# Revit family: tka-2200c-60_60Hz
name_source: partatom
category: 機械設備
units: mm (PartAtom-declared; Revit-internal decimal feet)

## family parameters
OmniClass タイトル = Heat Exchangers for Ventilation Air
OmniClass 番号 = 23.75.10.34.21
パーツ タイプ = 標準
ロード時にボイドで切り取り = いいえ
丸型コネクタ寸法 = 直径を使用
作業面ベース = いいえ
共有 = いいえ
常に垂直 = はい
部屋計算ポイント = はい

## types (1)
- TKA-2200C-60
    Clearance Front = 600
    Clearance Left = 600
    Clearance Top = 340  [stored 1.11549 ft]
    Depth = 897  [stored 2.94291 ft]
    EAサイズ_D = 0  [stored 0 ft]
    EAサイズ_W = 0  [stored 0 ft]
    Height = 380
    IfcExportAs = IfcAirToAirHeatRecoveryType
    IfcExportType = ROTARYWHEEL
    MAX静圧 = 0.0 Pa
    MAX風量 = 630.0 m³/h
    MIN静圧 = 0.0 Pa
    MIN風量 = 390.0 m³/h
    OAサイズ_D = 0  [stored 0 ft]
    OAサイズ_W = 0  [stored 0 ft]
    OmniClassCode = 23-27 23 19 11
    Panel_Depth = 960  [stored 3.14961 ft]
    Panel_Height = 15  [stored 0.0492126 ft]
    Panel_Width = 647  [stored 2.1227 ft]
    RAサイズ_D = 0  [stored 0 ft]
    SAサイズ_D = 0  [stored 0 ft]
    URL = https://www.mitsubishielectric.co.jp
    Uniclass2015Code = Pr_60_60_36_88
    Uniclass2015Title = Thermal wheels
    Uniclass2015Version = Systems v1.9
    Width = 604  [stored 1.98163 ft]
    エンタルピ交換効率_冷房 = 0.00%
    エンタルピ交換効率_暖房 = 0.00%
    ドレン管_Depth = 64
    ドレン管_H = 298  [stored 0.97769 ft]
    ドレン管_W = 420  [stored 1.37795 ft]
    ドレン管径 = 32 mm
    パネルマテリアル = 樹脂成形
    メンテナンススペース = はい
    モデル = TKA-2200C-60
    仕様書バージョン = Version1.0
    企業コード = 108420
    価格 = 298000 $
    分類コード = 50052504100080
    初期抵抗 = 0.0 Pa
    加湿給水管径 = 22 mm
    周波数 = 60 Hz
    呼称 = 加湿器
    外気量 = 0.0 m³/h
    天吊金具_幅 = 20  [stored 0.0656168 ft]
    天吊金具_径 = 7  [stored 0.0229659 ft]
    天吊金具_高さ = 100  [stored 0.328084 ft]
    天吊金具ピッチ1 = 664  [stored 2.17848 ft]
    天吊金具ピッチ2 = 897  [stored 2.94291 ft]
    実風量 = 0.0 m³/h
    形式 = 滴下浸透気化式
    排気量 = 0.0 m³/h
    有効加湿量 = 2.2
    本体マテリアル = 溶融亜鉛めっき鋼板
    極数 = 2
    構成部品 = インテリアパネル
    機外静圧 = 0.0 Pa
    機外静圧_排気 = 0.0 Pa
    法定耐用年数 = 15
    消費電力 = 102 W
    消費電力_加湿器 = 0 W
    温度交換効率 = 0.00%
    点検口 = はい
    点検口_Depth = 450  [stored 1.47638 ft]
    点検口離隔 = 150
    点検口高さ = 0  [stored 0 ft]
    相 = 1
    積算_科目 = 1 空気調和設備
    符号 = HUM
    給水管_Depth = 16  [stored 0.0524934 ft]
    給水管_H = 305  [stored 1.00066 ft]
    給水管_W = 314  [stored 1.03018 ft]
    製品リリース年月 = 2020/12/1
    製品出荷対象 = 国内
    製品質量 = 40.00 kg
    製造元 = MITSUBISHI ELECTRIC
    設置方法 = カセット形
    設計風量 = 0.0 m³/h
    説明 = 業務用単独加湿ユニット カセット形
    負荷分類 = 3_ファン類
    質量 = 48.00 kg
    運転質量 = 0.00 kg
    電動機出力 = 0 W
    電圧 = 100 V
    面風速 = 0.0 m/s
    風量 = 630.0 m³/h
    騒音レベル(dB(A)) = 39
    高さ調整可能範囲 = 60  [stored 0.19685 ft]

note: [stored X ft] marks values corroborated as IEEE doubles in the binary element streams (Revit-internal decimal feet)
